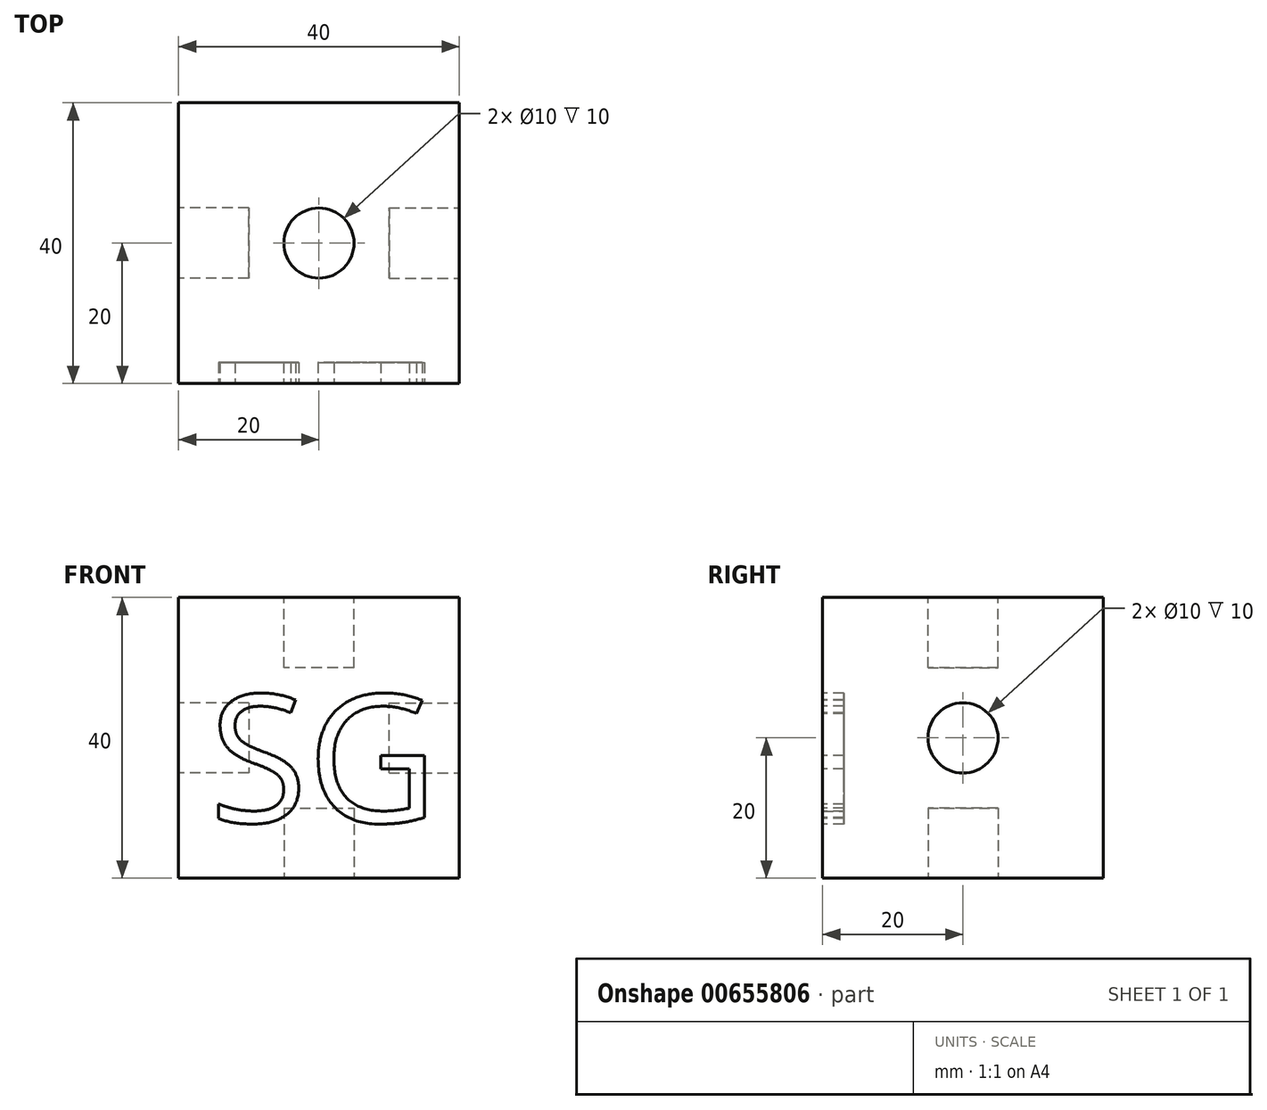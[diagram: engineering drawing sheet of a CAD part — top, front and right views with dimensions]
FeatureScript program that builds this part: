
annotation { "Feature Type Name" : "Feature", "Feature Type Description" : "" }
export const myFeature = defineFeature(function(context is Context, id is Id, definition is map)
    precondition{}
    {
        {
            var Q0;
            Q0=qCreatedBy(makeId("Front.planeOp"),FACE);
            var sketch = newSketch(context, id + "F0", { "sketchPlane" : qUnion([Q0])});
            skLineSegment(sketch, "E0", {"start": v(0, 0) * mm, "end": v(40, 0) * mm});
            skLineSegment(sketch, "E1", {"start": v(40, 0) * mm, "end": v(40, 40) * mm});
            skLineSegment(sketch, "E2", {"start": v(40, 40) * mm, "end": v(0, 40) * mm});
            skLineSegment(sketch, "E3", {"start": v(0, 40) * mm, "end": v(0, 0) * mm});
            skSolve(sketch);
        }
        {
            var Q0;
            Q0 = qSketchRegion(id + "F0", true);
            extrude(context, id + "F1", {"entities" : qUnion([Q0]), "depth" : 40 * mm, "offsetDistance" : 25 * mm});
        }
        {
            var Q0;
            Q0=makeQuery(id+"F1.opExtrude","CAP_FACE",FACE,{"disambiguationData":[OSD([sQuery(id+"F0.wireOp",EDGE,"E0"),sQuery(id+"F0.wireOp",EDGE,"E1"),sQuery(id+"F0.wireOp",EDGE,"E2"),sQuery(id+"F0.wireOp",EDGE,"E3")])],"isStart":false});
            var sketch = newSketch(context, id + "F2", { "sketchPlane" : qUnion([Q0])});
            skText(sketch, "E4", { "text": "SG", "fontName": "OpenSans-Regular.ttf"});
            const initialGuessF2  = {"E4": [0.00436, 0.00797, 1, 0, 0.01833]};
            skSetInitialGuess(sketch, initialGuessF2);
            skSolve(sketch);
        }
        {
            var Q0;
            Q0 = qSketchRegion(id + "F2", true);
            extrude(context, id + "F3", {"entities" : qUnion([Q0]), "operationType" : NewBodyOperationType.REMOVE, "oppositeDirection" : true, "depth" : 3 * mm, "offsetDistance" : 25 * mm});
        }
        {
            var Q0;
            Q0=makeQuery(id+"F1.opExtrude","SWEPT_FACE",FACE,{"disambiguationData":[OSD([sQuery(id+"F0.wireOp",EDGE,"E3")])]});
            var sketch = newSketch(context, id + "F4", { "sketchPlane" : qUnion([Q0])});
            skCircle(sketch, "E5", {"center": v(20, 20) * mm, "radius": 5 * mm});
            skPoint(sketch, "E5.centerSnap0", {"position": v(20, 40) * mm});
            skPoint(sketch, "E5.centerSnap1", {"position": v(0, 20) * mm});
            skSolve(sketch);
        }
        {
            var Q0;
            Q0 = qSketchRegion(id + "F4", true);
            extrude(context, id + "F5", {"entities" : qUnion([Q0]), "operationType" : NewBodyOperationType.REMOVE, "oppositeDirection" : true, "depth" : 10 * mm, "offsetDistance" : 25 * mm});
        }
        {
            var Q0;
            Q0=makeQuery(id+"F1.opExtrude","SWEPT_FACE",FACE,{"disambiguationData":[OSD([sQuery(id+"F0.wireOp",EDGE,"E1")])]});
            var sketch = newSketch(context, id + "F6", { "sketchPlane" : qUnion([Q0])});
            skCircle(sketch, "E6", {"center": v(-20, 20) * mm, "radius": 5 * mm});
            skPoint(sketch, "E6.centerSnap0", {"position": v(-40, 20) * mm});
            skPoint(sketch, "E6.centerSnap1", {"position": v(-20, 40) * mm});
            skSolve(sketch);
        }
        {
            var Q0;
            Q0 = qSketchRegion(id + "F6", true);
            extrude(context, id + "F7", {"entities" : qUnion([Q0]), "operationType" : NewBodyOperationType.REMOVE, "oppositeDirection" : true, "depth" : 10 * mm, "offsetDistance" : 25 * mm});
        }
        {
            var Q0;
            Q0=makeQuery(id+"F1.opExtrude","SWEPT_FACE",FACE,{"disambiguationData":[OSD([sQuery(id+"F0.wireOp",EDGE,"E2")])]});
            var sketch = newSketch(context, id + "F8", { "sketchPlane" : qUnion([Q0])});
            skCircle(sketch, "E7", {"center": v(20, -20) * mm, "radius": 5 * mm});
            skPoint(sketch, "E7.centerSnap0", {"position": v(40, -20) * mm});
            skPoint(sketch, "E7.centerSnap1", {"position": v(20, -40) * mm});
            skSolve(sketch);
        }
        {
            var Q0;
            Q0=makeQuery(id+"F8.imprint","IMPRINT",FACE,{"disambiguationData":[TD([[makeQuery(id+"F8.imprint","IMPRINT",EDGE,{"derivedFrom":sQuery(id+"F8.wireOp",EDGE,"E7")}),1.0]])]});
            extrude(context, id + "F9", {"entities" : qUnion([Q0]), "operationType" : NewBodyOperationType.REMOVE, "oppositeDirection" : true, "depth" : 10 * mm, "offsetDistance" : 25 * mm});
        }
        {
            var Q0;
            Q0=makeQuery(id+"F1.opExtrude","SWEPT_FACE",FACE,{"disambiguationData":[OSD([sQuery(id+"F0.wireOp",EDGE,"E0")])]});
            var sketch = newSketch(context, id + "F10", { "sketchPlane" : qUnion([Q0])});
            skCircle(sketch, "E8", {"center": v(20, 20) * mm, "radius": 5 * mm});
            skPoint(sketch, "E8.centerSnap0", {"position": v(0, 20) * mm});
            skPoint(sketch, "E8.centerSnap1", {"position": v(20, 40) * mm});
            skSolve(sketch);
        }
        {
            var Q0;
            Q0=makeQuery(id+"F10.imprint","IMPRINT",FACE,{"disambiguationData":[TD([[makeQuery(id+"F10.imprint","IMPRINT",EDGE,{"derivedFrom":sQuery(id+"F10.wireOp",EDGE,"E8")}),1.0]])]});
            extrude(context, id + "F11", {"entities" : qUnion([Q0]), "operationType" : NewBodyOperationType.REMOVE, "oppositeDirection" : true, "depth" : 10 * mm, "offsetDistance" : 25 * mm});
        }
    });
